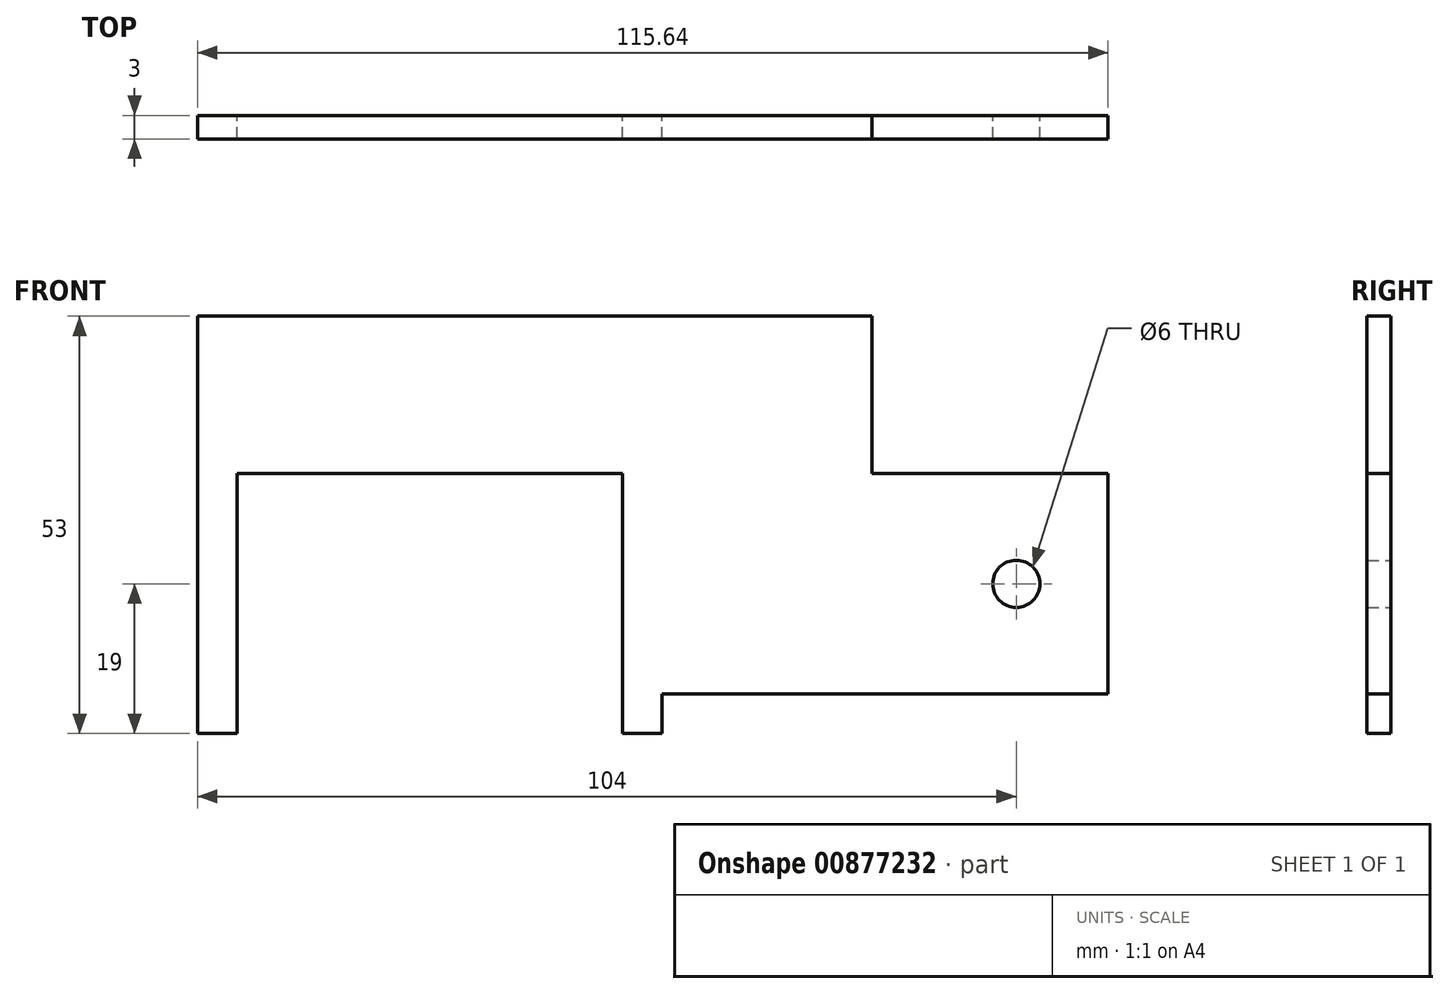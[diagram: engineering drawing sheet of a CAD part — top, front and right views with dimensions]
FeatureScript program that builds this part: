
annotation { "Feature Type Name" : "Feature", "Feature Type Description" : "" }
export const myFeature = defineFeature(function(context is Context, id is Id, definition is map)
    precondition{}
    {
        {
            var Q0;
            Q0=qCreatedBy(makeId("Front.planeOp"),FACE);
            var sketch = newSketch(context, id + "F0", { "sketchPlane" : qUnion([Q0])});
            skLineSegment(sketch, "E0.bottom", {"start": v(0, 20) * mm, "end": v(85.64, 20) * mm});
            skLineSegment(sketch, "E0.top", {"start": v(0, 0) * mm, "end": v(85.64, 0) * mm});
            skLineSegment(sketch, "E0.left", {"start": v(0, 20) * mm, "end": v(0, 0) * mm});
            skLineSegment(sketch, "E1.bottom", {"start": v(0, 20) * mm, "end": v(5, 20) * mm});
            skLineSegment(sketch, "E1.top", {"start": v(0, -33) * mm, "end": v(5, -33) * mm});
            skLineSegment(sketch, "E1.left", {"start": v(0, 20) * mm, "end": v(0, -33) * mm});
            skLineSegment(sketch, "E1.right", {"start": v(5, 20) * mm, "end": v(5, -33) * mm});
            skLineSegment(sketch, "E2.bottom", {"start": v(54, 20) * mm, "end": v(59, 20) * mm});
            skLineSegment(sketch, "E2.top", {"start": v(54, -33) * mm, "end": v(59, -33) * mm});
            skLineSegment(sketch, "E2.left", {"start": v(54, 20) * mm, "end": v(54, -33) * mm});
            skLineSegment(sketch, "E2.right", {"start": v(59, 20) * mm, "end": v(59, -33) * mm});
            skLineSegment(sketch, "E3.bottom", {"start": v(54, 0) * mm, "end": v(85.64, 0) * mm});
            skLineSegment(sketch, "E3.top", {"start": v(54, -28) * mm, "end": v(85.64, -28) * mm});
            skLineSegment(sketch, "E3.left", {"start": v(54, 0) * mm, "end": v(54, -28) * mm});
            skLineSegment(sketch, "E3.right", {"start": v(85.64, 0) * mm, "end": v(85.64, -28) * mm});
            skLineSegment(sketch, "E4.bottom", {"start": v(85.64, -28) * mm, "end": v(115.64, -28) * mm});
            skLineSegment(sketch, "E4.top", {"start": v(85.64, 0) * mm, "end": v(115.64, 0) * mm});
            skLineSegment(sketch, "E4.left", {"start": v(85.64, -28) * mm, "end": v(85.64, 0) * mm});
            skLineSegment(sketch, "E4.right", {"start": v(115.64, -28) * mm, "end": v(115.64, 0) * mm});
            skCircle(sketch, "E5", {"center": v(104, -14) * mm, "radius": 3 * mm});
            skLineSegment(sketch, "E6", {"start": v(85.64, 0) * mm, "end": v(85.64, 20) * mm});
            skSolve(sketch);
        }
        {
            var Q0;
            {var subQ0=sQuery(id+"F0.wireOp",EDGE,"E1.right");var subQ1=sQuery(id+"F0.wireOp",EDGE,"E0.bottom");var subQ2=makeQuery(id+"F0.imprint","INTERSECT",VERTEX,{"derivedFrom":[subQ1,subQ0]});Q0=makeQuery(id+"F0.imprint","IMPRINT",FACE,{"disambiguationData":[TD([[makeQuery(id+"F0.imprint","IMPRINT",EDGE,{"disambiguationData":[TD([[subQ2,-1.0]])],"derivedFrom":subQ1}),-1.0]])]});}
            var Q1;
            {var subQ3=sQuery(id+"F0.wireOp",EDGE,"E0.left");Q1=makeQuery(id+"F0.imprint","IMPRINT",FACE,{"disambiguationData":[TD([[makeQuery(id+"F0.imprint","IMPRINT",EDGE,{"derivedFrom":subQ3}),1.0]])]});}
            var Q2;
            {var subQ4=sQuery(id+"F0.wireOp",EDGE,"E1.top");Q2=makeQuery(id+"F0.imprint","IMPRINT",FACE,{"disambiguationData":[TD([[makeQuery(id+"F0.imprint","IMPRINT",EDGE,{"derivedFrom":subQ4}),1.0]])]});}
            var Q3;
            {var subQ0=sQuery(id+"F0.wireOp",EDGE,"E2.right");var subQ1=sQuery(id+"F0.wireOp",EDGE,"E0.bottom");var subQ2=makeQuery(id+"F0.imprint","INTERSECT",VERTEX,{"derivedFrom":[subQ1,subQ0]});Q3=makeQuery(id+"F0.imprint","IMPRINT",FACE,{"disambiguationData":[TD([[makeQuery(id+"F0.imprint","IMPRINT",EDGE,{"disambiguationData":[TD([[subQ2,1.0]])],"derivedFrom":subQ1}),-1.0]])]});}
            var Q4;
            {var subQ0=sQuery(id+"F0.wireOp",EDGE,"E2.right");var subQ1=sQuery(id+"F0.wireOp",EDGE,"E0.top");var subQ2=makeQuery(id+"F0.imprint","INTERSECT",VERTEX,{"derivedFrom":[subQ1,subQ0]});Q4=makeQuery(id+"F0.imprint","IMPRINT",FACE,{"disambiguationData":[TD([[makeQuery(id+"F0.imprint","IMPRINT",EDGE,{"disambiguationData":[TD([[subQ2,1.0]])],"derivedFrom":subQ1}),-1.0]])]});}
            var Q5;
            {var subQ0=sQuery(id+"F0.wireOp",EDGE,"E2.top");Q5=makeQuery(id+"F0.imprint","IMPRINT",FACE,{"disambiguationData":[TD([[makeQuery(id+"F0.imprint","IMPRINT",EDGE,{"derivedFrom":subQ0}),1.0]])]});}
            var Q6;
            {var subQ5=sQuery(id+"F0.wireOp",EDGE,"E3.right");Q6=makeQuery(id+"F0.imprint","IMPRINT",FACE,{"disambiguationData":[TD([[makeQuery(id+"F0.imprint","IMPRINT",EDGE,{"derivedFrom":subQ5}),-1.0]])]});}
            var Q7;
            {var subQ10=sQuery(id+"F0.wireOp",EDGE,"ACqgj5Fc-D6B9-wPeG-Lqm1-0azibA2jnmIg.bottom");Q7=makeQuery(id+"F0.imprint","IMPRINT",FACE,{"disambiguationData":[TD([[makeQuery(id+"F0.imprint","IMPRINT",EDGE,{"derivedFrom":subQ10}),1.0]])]});}
            var Q8;
            {var subQ3=sQuery(id+"F0.wireOp",EDGE,"E6");Q8=makeQuery(id+"F0.imprint","IMPRINT",FACE,{"disambiguationData":[TD([[makeQuery(id+"F0.imprint","IMPRINT",EDGE,{"derivedFrom":subQ3}),1.0]])]});}
            var Q9;
            {var subQ3=sQuery(id+"F0.wireOp",EDGE,"E3.right");Q9=makeQuery(id+"F0.imprint","IMPRINT",FACE,{"disambiguationData":[TD([[makeQuery(id+"F0.imprint","IMPRINT",EDGE,{"derivedFrom":subQ3}),-1.0]])]});}
            var Q10;
            Q10=makeQuery(id+"F0.imprint","IMPRINT",FACE,{"disambiguationData":[TD([[makeQuery(id+"F0.imprint","IMPRINT",EDGE,{"derivedFrom":sQuery(id+"F0.wireOp",EDGE,"E3.right")}),1.0]])]});
            extrude(context, id + "F1", {"entities" : qUnion([Q0, Q1, Q2, Q3, Q4, Q5, Q6, Q7, Q8, Q9, Q10]), "depth" : 3 * mm, "offsetDistance" : 25 * mm});
        }
    });
